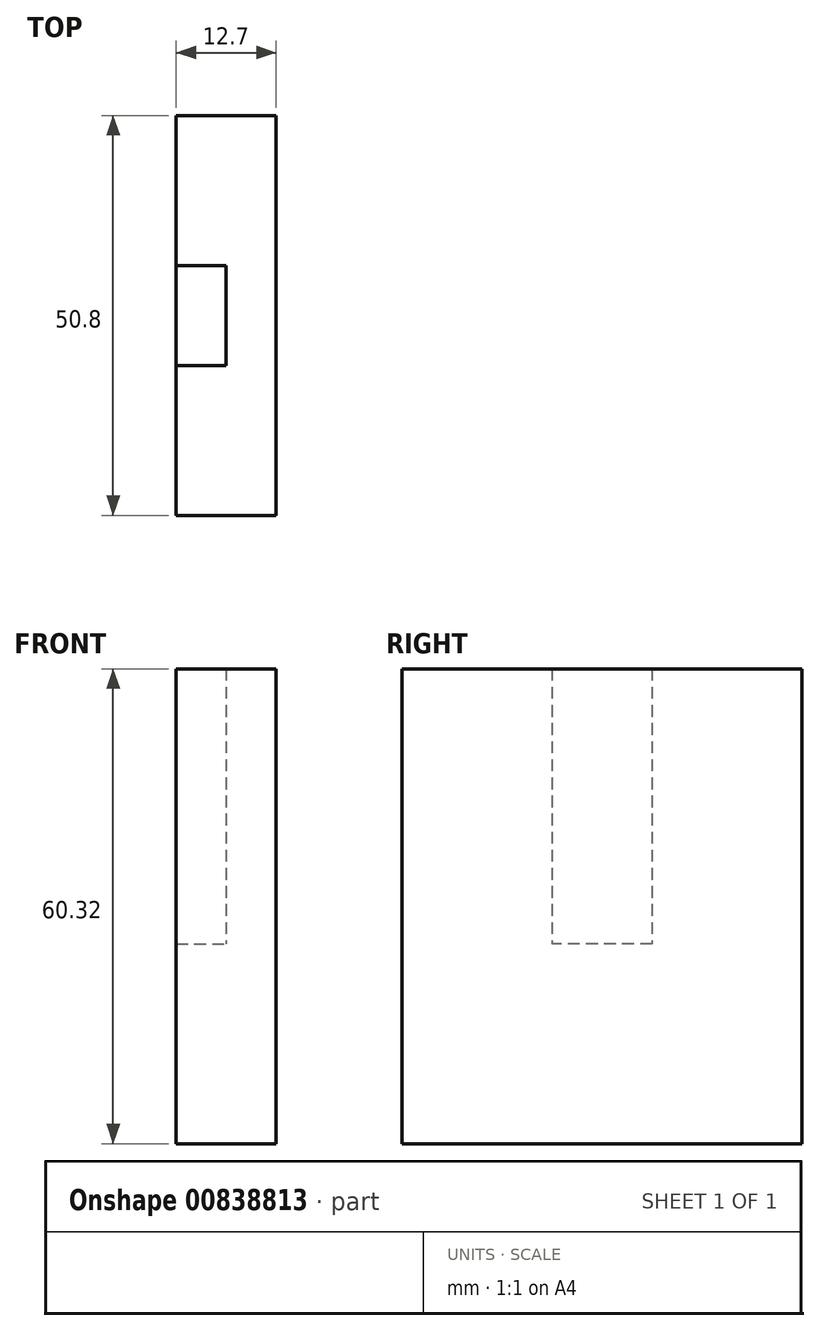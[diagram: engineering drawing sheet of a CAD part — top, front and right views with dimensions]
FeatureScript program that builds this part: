
annotation { "Feature Type Name" : "Feature", "Feature Type Description" : "" }
export const myFeature = defineFeature(function(context is Context, id is Id, definition is map)
    precondition{}
    {
        {
            var Q0;
            Q0=qCreatedBy(makeId("Top.planeOp"),FACE);
            var sketch = newSketch(context, id + "F0", { "sketchPlane" : qUnion([Q0])});
            skLineSegment(sketch, "E0.bottom", {"start": v(6.35, -25.4) * mm, "end": v(-6.35, -25.4) * mm});
            skLineSegment(sketch, "E0.top", {"start": v(6.35, 25.4) * mm, "end": v(-6.35, 25.4) * mm});
            skLineSegment(sketch, "E0.left", {"start": v(6.35, -25.4) * mm, "end": v(6.35, 25.4) * mm});
            skLineSegment(sketch, "E0.right", {"start": v(-6.35, -25.4) * mm, "end": v(-6.35, 25.4) * mm});
            skPoint(sketch, "E0.middle", {"position": v(0, 0) * mm});
            skLineSegment(sketch, "E1.bottom", {"start": v(-6.35, 6.35) * mm, "end": v(0, 6.35) * mm});
            skLineSegment(sketch, "E1.top", {"start": v(-6.35, -6.35) * mm, "end": v(0, -6.35) * mm});
            skLineSegment(sketch, "E1.left", {"start": v(-6.35, 6.35) * mm, "end": v(-6.35, -6.35) * mm});
            skLineSegment(sketch, "E1.right", {"start": v(0, 6.35) * mm, "end": v(0, -6.35) * mm});
            skSolve(sketch);
        }
        {
            var Q0;
            {var subQ1=sQuery(id+"F0.wireOp",EDGE,"E0.bottom");Q0=makeQuery(id+"F0.imprint","IMPRINT",FACE,{"disambiguationData":[TD([[makeQuery(id+"F0.imprint","IMPRINT",EDGE,{"derivedFrom":subQ1}),-1.0]])]});}
            extrude(context, id + "F1", {"entities" : qUnion([Q0]), "depth" : 60.32 * mm, "offsetDistance" : 25.4 * mm});
        }
        {
            var Q0;
            {var subQ0=sQuery(id+"F0.wireOp",EDGE,"E1.bottom");Q0=makeQuery(id+"F0.imprint","IMPRINT",FACE,{"disambiguationData":[TD([[makeQuery(id+"F0.imprint","IMPRINT",EDGE,{"derivedFrom":subQ0}),-1.0]])]});}
            extrude(context, id + "F2", {"entities" : qUnion([Q0]), "operationType" : NewBodyOperationType.ADD, "depth" : 25.4 * mm, "offsetDistance" : 25.4 * mm});
        }
    });
